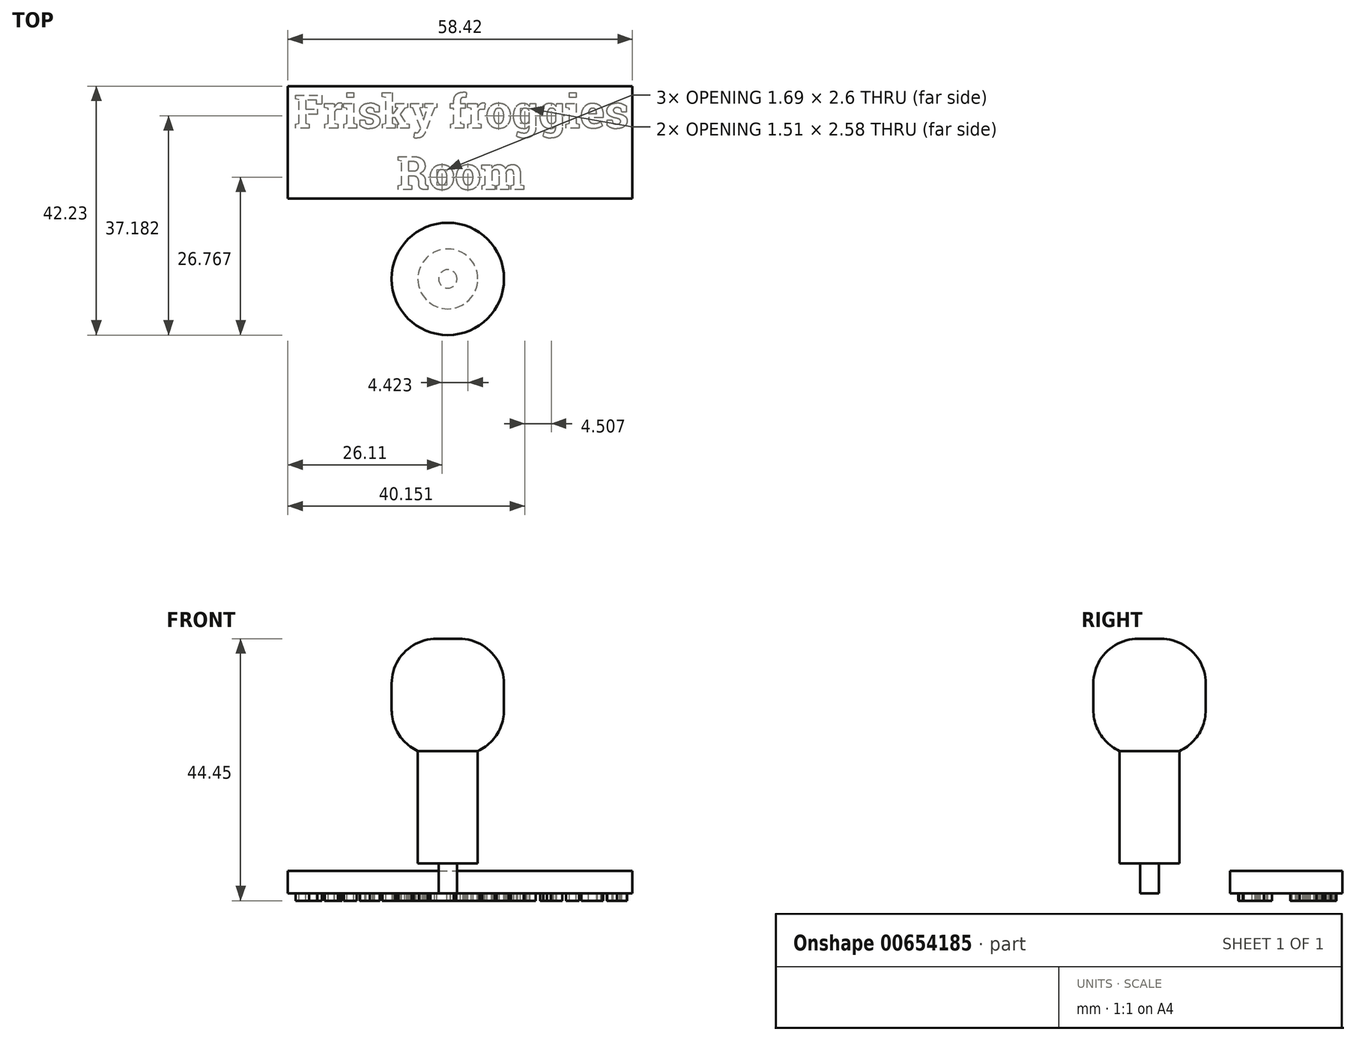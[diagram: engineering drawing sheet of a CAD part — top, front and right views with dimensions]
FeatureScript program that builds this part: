
annotation { "Feature Type Name" : "Feature", "Feature Type Description" : "" }
export const myFeature = defineFeature(function(context is Context, id is Id, definition is map)
    precondition{}
    {
        {
            var Q0;
            Q0=qCreatedBy(makeId("Top.planeOp"),FACE);
            var sketch = newSketch(context, id + "F0", { "sketchPlane" : qUnion([Q0])});
            skText(sketch, "E0", { "text": "Frisky froggies \n         Room", "fontName": "RobotoSlab-Bold.ttf"});
            const initialGuessF0  = {"E0": [-0.02604, 0.02557, 1, 0, 0.00568]};
            skSetInitialGuess(sketch, initialGuessF0);
            skSolve(sketch);
        }
        {
            var Q0;
            Q0=qSketchRegion(id+"F0",true);
            extrude(context, id + "F1", {"entities" : qUnion([Q0]), "oppositeDirection" : true, "depth" : 1.27 * mm, "offsetDistance" : 25.4 * mm});
        }
        {
            var Q0;
            Q0=qCreatedBy(makeId("Top.planeOp"),FACE);
            var sketch = newSketch(context, id + "F2", { "sketchPlane" : qUnion([Q0])});
            skLineSegment(sketch, "E1.bottom", {"start": v(-27.11, 32.7) * mm, "end": v(31.3, 32.7) * mm});
            skLineSegment(sketch, "E1.top", {"start": v(-27.11, 13.65) * mm, "end": v(31.3, 13.65) * mm});
            skLineSegment(sketch, "E1.left", {"start": v(-27.11, 32.7) * mm, "end": v(-27.11, 13.65) * mm});
            skLineSegment(sketch, "E1.right", {"start": v(31.3, 32.7) * mm, "end": v(31.3, 13.65) * mm});
            skSolve(sketch);
        }
        {
            var Q0;
            Q0=makeQuery(id+"F2.imprint","IMPRINT",FACE,{"disambiguationData":[TD([[makeQuery(id+"F2.imprint","IMPRINT",EDGE,{"derivedFrom":sQuery(id+"F2.wireOp",EDGE,"E1.bottom")}),-1.0]])]});
            extrude(context, id + "F3", {"entities" : qUnion([Q0]), "depth" : 3.8 * mm, "offsetDistance" : 25.4 * mm});
        }
        {
            var Q0;
            Q0=makeQuery(id+"F3.opExtrude","CAP_FACE",FACE,{"disambiguationData":[OSD([sQuery(id+"F2.wireOp",EDGE,"E1.bottom"),sQuery(id+"F2.wireOp",EDGE,"E1.top"),sQuery(id+"F2.wireOp",EDGE,"E1.left"),sQuery(id+"F2.wireOp",EDGE,"E1.right")])],"isStart":false});
            var sketch = newSketch(context, id + "F4", { "sketchPlane" : qUnion([Q0])});
            skCircle(sketch, "E2", {"center": v(0.7, 23.18) * mm, "radius": 3.18 * mm});
            skPoint(sketch, "E2.centerSnap0", {"position": v(-27.11, 23.18) * mm});
            skSolve(sketch);
        }
        {
            var Q0;
            Q0=makeQuery(id+"F4.imprint","IMPRINT",FACE,{"disambiguationData":[TD([[makeQuery(id+"F4.imprint","IMPRINT",EDGE,{"derivedFrom":sQuery(id+"F4.wireOp",EDGE,"E2")}),1.0]])]});
            extrude(context, id + "F5", {"entities" : qUnion([Q0]), "operationType" : NewBodyOperationType.ADD, "oppositeDirection" : true, "depth" : 3.8 * mm, "offsetDistance" : 25.4 * mm});
        }
        {
            var Q0;
            Q0=sQuery(id+"F4.wireOp",VERTEX,"E2.center");
            var Q1;
            Q1=makeQuery(id+"F3.opExtrude","SWEPT_BODY",BODY,{"disambiguationData":[OSD([sQuery(id+"F2.wireOp",EDGE,"E1.bottom"),sQuery(id+"F2.wireOp",EDGE,"E1.top"),sQuery(id+"F2.wireOp",EDGE,"E1.left"),sQuery(id+"F2.wireOp",EDGE,"E1.right")])]});
            var Q2;
            Q2=makeQuery(id+"F1.opExtrude","SWEPT_BODY",BODY,{"disambiguationData":[OSD([sQuery(id+"F0.wireOp",EDGE,"E0.sketch_text.stroke-65"),sQuery(id+"F0.wireOp",EDGE,"E0.sketch_text.stroke-66"),sQuery(id+"F0.wireOp",EDGE,"E0.sketch_text.stroke-67"),sQuery(id+"F0.wireOp",EDGE,"E0.sketch_text.stroke-68"),sQuery(id+"F0.wireOp",EDGE,"E0.sketch_text.stroke-69"),sQuery(id+"F0.wireOp",EDGE,"E0.sketch_text.stroke-70"),sQuery(id+"F0.wireOp",EDGE,"E0.sketch_text.stroke-71"),sQuery(id+"F0.wireOp",EDGE,"E0.sketch_text.stroke-72"),sQuery(id+"F0.wireOp",EDGE,"E0.sketch_text.stroke-73"),sQuery(id+"F0.wireOp",EDGE,"E0.sketch_text.stroke-74"),sQuery(id+"F0.wireOp",EDGE,"E0.sketch_text.stroke-75"),sQuery(id+"F0.wireOp",EDGE,"E0.sketch_text.stroke-76"),sQuery(id+"F0.wireOp",EDGE,"E0.sketch_text.stroke-77"),sQuery(id+"F0.wireOp",EDGE,"E0.sketch_text.stroke-78"),sQuery(id+"F0.wireOp",EDGE,"E0.sketch_text.stroke-79"),sQuery(id+"F0.wireOp",EDGE,"E0.sketch_text.stroke-80")])]});
            hole(context, id + "F6", {"style" : HoleStyle.SIMPLE, "endStyle" : HoleEndStyle.THROUGH, "holeDiameter" : 3.17 * mm, "majorDiameter" : 6.35 * mm, "isTappedThrough" : true, "tappedDepth" : 12.7 * mm, "tapClearance" : 3, "locations" : qUnion([Q0]), "scope" : qUnion([Q1, Q2])});
        }
        {
            var Q0;
            Q0=qCreatedBy(makeId("Top.planeOp"),FACE);
            var sketch = newSketch(context, id + "F7", { "sketchPlane" : qUnion([Q0])});
            skCircle(sketch, "E3", {"center": v(0, 0) * mm, "radius": 1.56 * mm});
            skSolve(sketch);
        }
        {
            var Q0;
            Q0=qSketchRegion(id+"F7",true);
            var sketch = newSketch(context, id + "F8", { "sketchPlane" : qUnion([Q0])});
            skSolve(sketch);
        }
        {
            var Q0;
            Q0=qSketchRegion(id+"F8",true);
            var Q1;
            Q1=makeQuery(id+"F8.imprint","IMPRINT",FACE,{"disambiguationData":[TD([[makeQuery(id+"F8.imprint","IMPRINT",EDGE,{"derivedFrom":makeQuery(id+"F7.imprint","IMPRINT",EDGE,{"derivedFrom":sQuery(id+"F7.wireOp",EDGE,"E3")})}),1.0]])]});
            extrude(context, id + "F9", {"entities" : qUnion([Q0, Q1]), "depth" : 5.08 * mm, "offsetDistance" : 25.4 * mm});
        }
        {
            var Q0;
            Q0=makeQuery(id+"F9.opExtrude","CAP_FACE",FACE,{"disambiguationData":[OSD([sQuery(id+"F7.wireOp",EDGE,"E3")])],"isStart":false});
            var sketch = newSketch(context, id + "F10", { "sketchPlane" : qUnion([Q0])});
            skCircle(sketch, "E4", {"center": v(0, 0) * mm, "radius": 5.08 * mm});
            skSolve(sketch);
        }
        {
            var Q0;
            Q0=makeQuery(id+"F10.imprint","IMPRINT",FACE,{"disambiguationData":[TD([[makeQuery(id+"F10.imprint","IMPRINT",EDGE,{"derivedFrom":sQuery(id+"F10.wireOp",EDGE,"E4")}),1.0]])]});
            var Q1;
            Q1=makeQuery(id+"F10.imprint","IMPRINT",FACE,{"disambiguationData":[TD([[makeQuery(id+"F10.imprint","IMPRINT",EDGE,{"derivedFrom":makeQuery(id+"F9.opExtrude","CAP_EDGE",EDGE,{"disambiguationData":[OSD([sQuery(id+"F7.wireOp",EDGE,"E3")])],"isStart":false})}),1.0]])]});
            var Q2;
            Q2=sQuery(id+"F10.wireOp",EDGE,"E4");
            extrude(context, id + "F11", {"entities" : qUnion([Q0, Q1]), "surfaceEntities" : qUnion([Q2]), "depth" : 19.05 * mm, "offsetDistance" : 25.4 * mm});
        }
        {
            var Q0;
            Q0=makeQuery(id+"F11.opExtrude","CAP_FACE",FACE,{"disambiguationData":[OSD([sQuery(id+"F10.wireOp",EDGE,"E4")])],"isStart":false});
            var sketch = newSketch(context, id + "F12", { "sketchPlane" : qUnion([Q0])});
            skCircle(sketch, "E5", {"center": v(0, 0) * mm, "radius": 9.53 * mm});
            skSolve(sketch);
        }
        {
            var Q0;
            Q0=makeQuery(id+"F12.imprint","IMPRINT",FACE,{"disambiguationData":[TD([[makeQuery(id+"F12.imprint","IMPRINT",EDGE,{"derivedFrom":sQuery(id+"F12.wireOp",EDGE,"E5")}),1.0]])]});
            var Q1;
            Q1=makeQuery(id+"F12.imprint","IMPRINT",FACE,{"disambiguationData":[TD([[makeQuery(id+"F12.imprint","IMPRINT",EDGE,{"derivedFrom":makeQuery(id+"F11.opExtrude","CAP_EDGE",EDGE,{"disambiguationData":[OSD([sQuery(id+"F10.wireOp",EDGE,"E4")])],"isStart":false})}),1.0]])]});
            extrude(context, id + "F13", {"entities" : qUnion([Q0, Q1]), "operationType" : NewBodyOperationType.ADD, "depth" : 19.05 * mm, "offsetDistance" : 25.4 * mm});
        }
        {
            var Q0;
            Q0=makeQuery(id+"F13.opExtrude","CAP_EDGE",EDGE,{"disambiguationData":[OSD([sQuery(id+"F12.wireOp",EDGE,"E5")])],"isStart":true});
            var Q1;
            Q1=makeQuery(id+"F13.opExtrude","CAP_EDGE",EDGE,{"disambiguationData":[OSD([sQuery(id+"F12.wireOp",EDGE,"E5")])],"isStart":false});
            fillet(context, id + "F14", {"entities" : qUnion([Q0, Q1]), "radius" : 7.62 * mm, "tangentPropagation" : true, "allowEdgeOverflow" : false});
        }
    });
